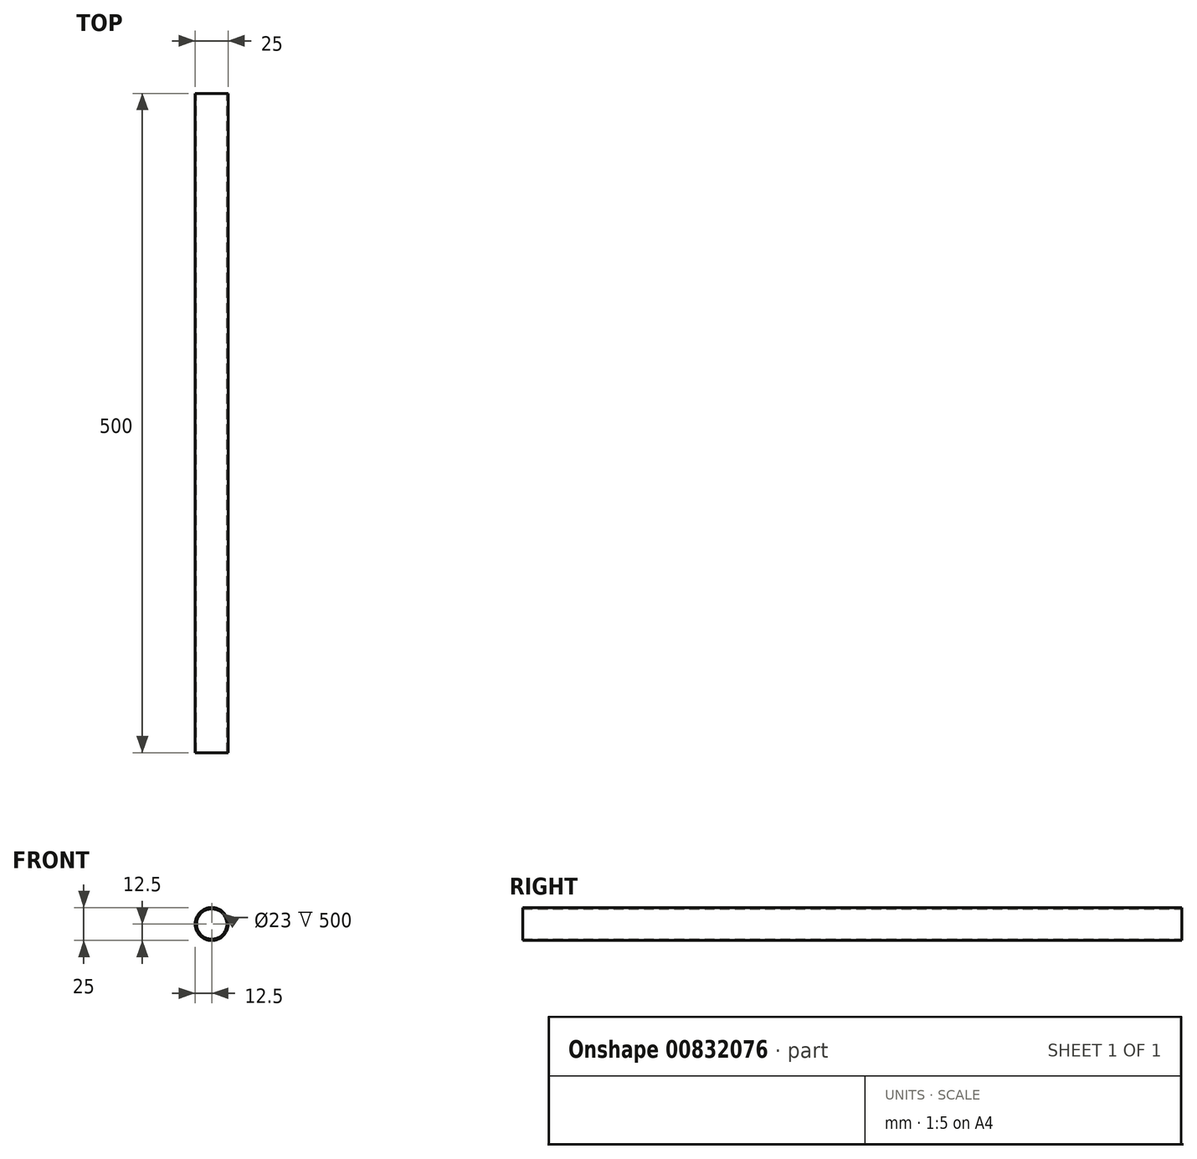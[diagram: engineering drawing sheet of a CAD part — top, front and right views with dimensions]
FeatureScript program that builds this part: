
annotation { "Feature Type Name" : "Feature", "Feature Type Description" : "" }
export const myFeature = defineFeature(function(context is Context, id is Id, definition is map)
    precondition{}
    {
        {
            var Q0;
            Q0=qCreatedBy(makeId("Front.planeOp"),FACE);
            var sketch = newSketch(context, id + "F0", { "sketchPlane" : qUnion([Q0])});
            skCircle(sketch, "E0", {"center": v(0, 0) * mm, "radius": 12.5 * mm});
            skCircle(sketch, "E1", {"center": v(0, 0) * mm, "radius": 11.5 * mm});
            skSolve(sketch);
        }
        {
            var Q0;
            Q0 = qSketchRegion(id + "F0", true);
            extrude(context, id + "F1", {"entities" : qUnion([Q0]), "endBound" : BoundingType.SYMMETRIC, "depth" : 500 * mm, "offsetDistance" : 25 * mm});
        }
    });
